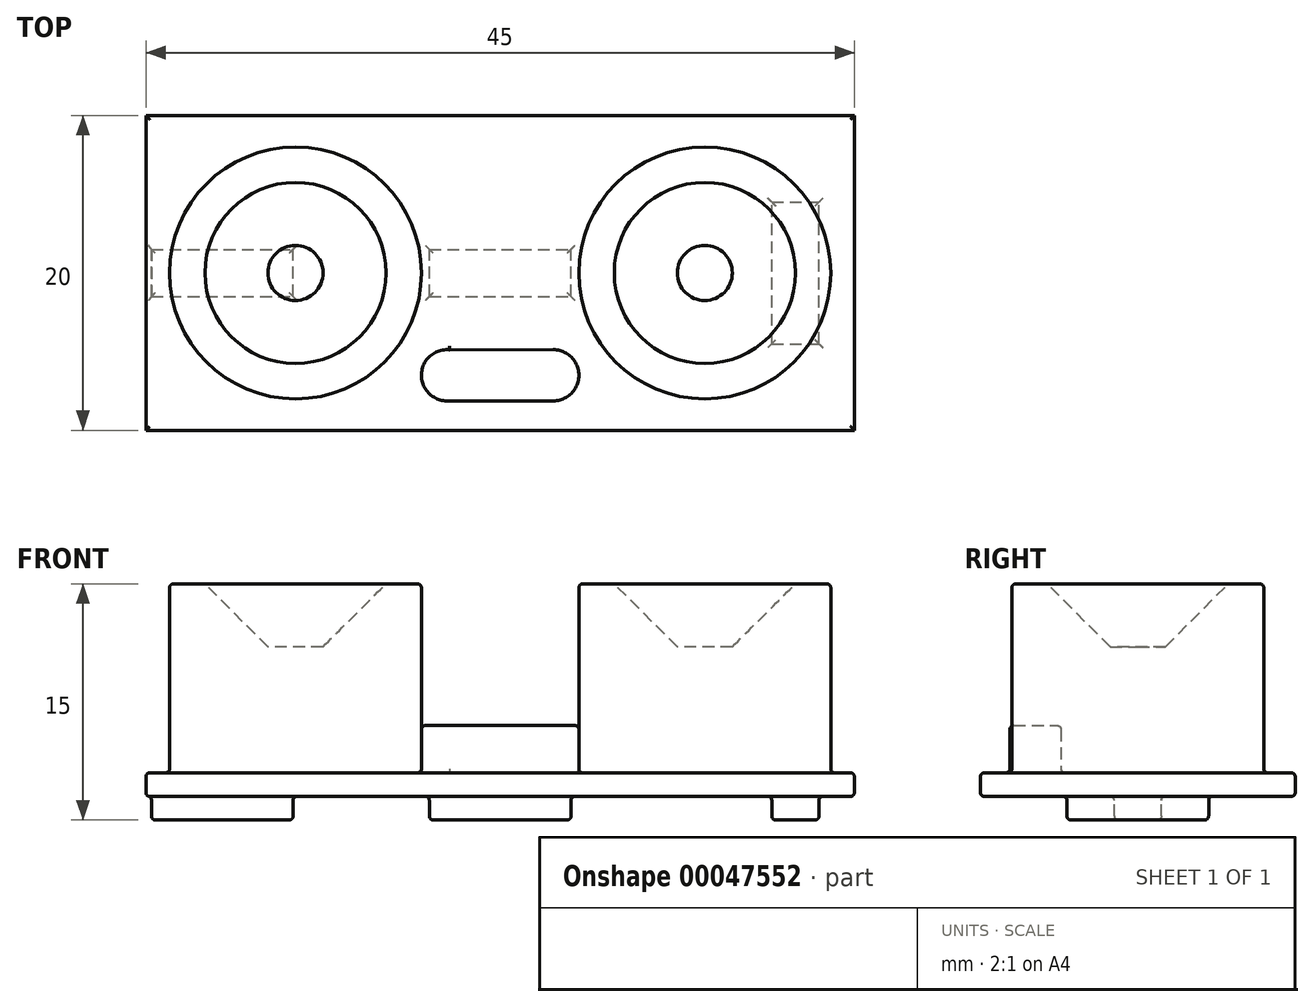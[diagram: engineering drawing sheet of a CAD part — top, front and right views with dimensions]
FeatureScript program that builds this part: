
annotation { "Feature Type Name" : "Feature", "Feature Type Description" : "" }
export const myFeature = defineFeature(function(context is Context, id is Id, definition is map)
    precondition{}
    {
        {
            var Q0;
            Q0=qCreatedBy(makeId("Top.planeOp"),FACE);
            var sketch = newSketch(context, id + "F0", { "sketchPlane" : qUnion([Q0])});
            skLineSegment(sketch, "E0.bottom", {"start": v(-22.5, 10) * mm, "end": v(22.5, 10) * mm});
            skLineSegment(sketch, "E0.top", {"start": v(-22.5, -10) * mm, "end": v(22.5, -10) * mm});
            skLineSegment(sketch, "E0.left", {"start": v(-22.5, 10) * mm, "end": v(-22.5, -10) * mm});
            skLineSegment(sketch, "E0.right", {"start": v(22.5, 10) * mm, "end": v(22.5, -10) * mm});
            skSolve(sketch);
        }
        {
            var Q0;
            Q0 = qSketchRegion(id + "F0", true);
            extrude(context, id + "F1", {"entities" : qUnion([Q0]), "depth" : 1.5 * mm});
        }
        {
            var Q0;
            Q0=makeQuery(id+"F1.opExtrude","CAP_FACE",FACE,{"disambiguationData":[OSD([sQuery(id+"F0.wireOp",EDGE,"E0.bottom"),sQuery(id+"F0.wireOp",EDGE,"E0.top"),sQuery(id+"F0.wireOp",EDGE,"E0.left"),sQuery(id+"F0.wireOp",EDGE,"E0.right")])],"isStart":false});
            var sketch = newSketch(context, id + "F2", { "sketchPlane" : qUnion([Q0])});
            skCircle(sketch, "E1", {"center": v(-13, 0) * mm, "radius": 8 * mm});
            skCircle(sketch, "E2", {"center": v(13, 0) * mm, "radius": 8 * mm});
            skSolve(sketch);
        }
        {
            var Q0;
            Q0 = qSketchRegion(id + "F2", true);
            extrude(context, id + "F3", {"entities" : qUnion([Q0]), "operationType" : NewBodyOperationType.ADD, "depth" : 12 * mm});
        }
        {
            var Q0;
            Q0=makeQuery(id+"F1.opExtrude","CAP_FACE",FACE,{"disambiguationData":[OSD([sQuery(id+"F0.wireOp",EDGE,"E0.bottom"),sQuery(id+"F0.wireOp",EDGE,"E0.top"),sQuery(id+"F0.wireOp",EDGE,"E0.left"),sQuery(id+"F0.wireOp",EDGE,"E0.right")])],"isStart":false});
            var sketch = newSketch(context, id + "F4", { "sketchPlane" : qUnion([Q0])});
            skArc(sketch, "E3", {"start": v(-3.22, -4.88) * mm, "mid": v(-5, -6.42) * mm, "end": v(-3.38, -8.12) * mm});
            skArc(sketch, "E4", {"start": v(3.38, -8.12) * mm, "mid": v(5, -6.5) * mm, "end": v(3.37, -4.88) * mm});
            skLineSegment(sketch, "E5", {"start": v(-3.54, -4.88) * mm, "end": v(3.38, -4.88) * mm});
            skLineSegment(sketch, "E6", {"start": v(-3.37, -8.12) * mm, "end": v(3.38, -8.12) * mm});
            skSolve(sketch);
        }
        {
            var Q0;
            Q0 = qSketchRegion(id + "F4", true);
            extrude(context, id + "F5", {"entities" : qUnion([Q0]), "operationType" : NewBodyOperationType.ADD, "depth" : 3 * mm});
        }
        {
            var Q0;
            Q0=makeQuery(id+"F3.opExtrude","CAP_FACE",FACE,{"disambiguationData":[OSD([sQuery(id+"F2.wireOp",EDGE,"E1")])],"isStart":false});
            var Q1;
            Q1=makeQuery(id+"F3.opExtrude","CAP_FACE",FACE,{"disambiguationData":[OSD([sQuery(id+"F2.wireOp",EDGE,"E2")])],"isStart":false});
            fillet(context, id + "F6", {"entities" : qUnion([Q0, Q1]), "radius" : .25 * mm, "tangentPropagation" : true, "allowEdgeOverflow" : false});
        }
        {
            var Q0;
            Q0=makeQuery(id+"F5.opExtrude","CAP_FACE",FACE,{"disambiguationData":[OSD([sQuery(id+"F4.wireOp",EDGE,"E3"),sQuery(id+"F4.wireOp",EDGE,"E4"),sQuery(id+"F4.wireOp",EDGE,"E5"),sQuery(id+"F4.wireOp",EDGE,"E6")])],"isStart":false});
            var Q1;
            Q1=makeQuery(id+"F5.opExtrude","SWEPT_FACE",FACE,{"disambiguationData":[OSD([sQuery(id+"F4.wireOp",EDGE,"E3")])]});
            var Q2;
            Q2=makeQuery(id+"F5.opExtrude","SWEPT_FACE",FACE,{"disambiguationData":[OSD([sQuery(id+"F4.wireOp",EDGE,"E6")])]});
            var Q3;
            Q3=makeQuery(id+"F5.opExtrude","SWEPT_FACE",FACE,{"disambiguationData":[OSD([sQuery(id+"F4.wireOp",EDGE,"E5")])]});
            var Q4;
            Q4=makeQuery(id+"F5.opExtrude","SWEPT_FACE",FACE,{"disambiguationData":[OSD([sQuery(id+"F4.wireOp",EDGE,"E4")])]});
            var Q5;
            Q5=makeQuery(id+"F3.opExtrude","SWEPT_FACE",FACE,{"disambiguationData":[OSD([sQuery(id+"F2.wireOp",EDGE,"E1")])]});
            var Q6;
            Q6=makeQuery(id+"F3.opExtrude","SWEPT_FACE",FACE,{"disambiguationData":[OSD([sQuery(id+"F2.wireOp",EDGE,"E2")])]});
            fillet(context, id + "F7", {"entities" : qUnion([Q0, Q1, Q2, Q3, Q4, Q5, Q6]), "radius" : .25 * mm, "tangentPropagation" : true, "allowEdgeOverflow" : false});
        }
        {
            var Q0;
            Q0=makeQuery(id+"F1.opExtrude","CAP_FACE",FACE,{"disambiguationData":[OSD([sQuery(id+"F0.wireOp",EDGE,"E0.bottom"),sQuery(id+"F0.wireOp",EDGE,"E0.top"),sQuery(id+"F0.wireOp",EDGE,"E0.left"),sQuery(id+"F0.wireOp",EDGE,"E0.right")])],"isStart":false});
            var Q1;
            Q1=makeQuery(id+"F1.opExtrude","CAP_FACE",FACE,{"disambiguationData":[OSD([sQuery(id+"F0.wireOp",EDGE,"E0.bottom"),sQuery(id+"F0.wireOp",EDGE,"E0.top"),sQuery(id+"F0.wireOp",EDGE,"E0.left"),sQuery(id+"F0.wireOp",EDGE,"E0.right")])],"isStart":true});
            fillet(context, id + "F8", {"entities" : qUnion([Q0, Q1]), "radius" : .25 * mm, "tangentPropagation" : true, "allowEdgeOverflow" : false});
        }
        {
            var Q0;
            Q0=makeQuery(id+"F1.opExtrude","CAP_FACE",FACE,{"disambiguationData":[OSD([sQuery(id+"F0.wireOp",EDGE,"E0.bottom"),sQuery(id+"F0.wireOp",EDGE,"E0.top"),sQuery(id+"F0.wireOp",EDGE,"E0.left"),sQuery(id+"F0.wireOp",EDGE,"E0.right")])],"isStart":true});
            var sketch = newSketch(context, id + "F9", { "sketchPlane" : qUnion([Q0])});
            skLineSegment(sketch, "E7.bottom", {"start": v(-4.5, 1.5) * mm, "end": v(4.5, 1.5) * mm});
            skLineSegment(sketch, "E7.top", {"start": v(-4.5, -1.5) * mm, "end": v(4.5, -1.5) * mm});
            skLineSegment(sketch, "E7.left", {"start": v(-4.5, 1.5) * mm, "end": v(-4.5, -1.5) * mm});
            skLineSegment(sketch, "E7.right", {"start": v(4.5, 1.5) * mm, "end": v(4.5, -1.5) * mm});
            skLineSegment(sketch, "E8.bottom", {"start": v(17.25, 4.5) * mm, "end": v(20.25, 4.5) * mm});
            skLineSegment(sketch, "E8.top", {"start": v(17.25, -4.5) * mm, "end": v(20.25, -4.5) * mm});
            skLineSegment(sketch, "E8.left", {"start": v(17.25, 4.5) * mm, "end": v(17.25, -4.5) * mm});
            skLineSegment(sketch, "E8.right", {"start": v(20.25, 4.5) * mm, "end": v(20.25, -4.5) * mm});
            skLineSegment(sketch, "E9.bottom", {"start": v(-22.15, 1.5) * mm, "end": v(-13.15, 1.5) * mm});
            skLineSegment(sketch, "E9.top", {"start": v(-22.15, -1.5) * mm, "end": v(-13.15, -1.5) * mm});
            skLineSegment(sketch, "E9.left", {"start": v(-22.15, 1.5) * mm, "end": v(-22.15, -1.5) * mm});
            skLineSegment(sketch, "E9.right", {"start": v(-13.15, 1.5) * mm, "end": v(-13.15, -1.5) * mm});
            skSolve(sketch);
        }
        {
            var Q0;
            Q0 = qSketchRegion(id + "F9", true);
            extrude(context, id + "F10", {"entities" : qUnion([Q0]), "operationType" : NewBodyOperationType.ADD, "depth" : 1.5 * mm});
        }
        {
            var Q0;
            Q0=makeQuery(id+"F1.opExtrude","CAP_FACE",FACE,{"disambiguationData":[OSD([sQuery(id+"F0.wireOp",EDGE,"E0.bottom"),sQuery(id+"F0.wireOp",EDGE,"E0.top"),sQuery(id+"F0.wireOp",EDGE,"E0.left"),sQuery(id+"F0.wireOp",EDGE,"E0.right")])],"isStart":true});
            var Q1;
            Q1=makeQuery(id+"F10.opExtrude","CAP_FACE",FACE,{"disambiguationData":[OSD([sQuery(id+"F9.wireOp",EDGE,"E9.bottom"),sQuery(id+"F9.wireOp",EDGE,"E9.top"),sQuery(id+"F9.wireOp",EDGE,"E9.left"),sQuery(id+"F9.wireOp",EDGE,"E9.right")])],"isStart":false});
            var Q2;
            Q2=makeQuery(id+"F10.opExtrude","CAP_FACE",FACE,{"disambiguationData":[OSD([sQuery(id+"F9.wireOp",EDGE,"E7.bottom"),sQuery(id+"F9.wireOp",EDGE,"E7.top"),sQuery(id+"F9.wireOp",EDGE,"E7.left"),sQuery(id+"F9.wireOp",EDGE,"E7.right")])],"isStart":false});
            var Q3;
            Q3=makeQuery(id+"F10.opExtrude","CAP_FACE",FACE,{"disambiguationData":[OSD([sQuery(id+"F9.wireOp",EDGE,"E8.bottom"),sQuery(id+"F9.wireOp",EDGE,"E8.top"),sQuery(id+"F9.wireOp",EDGE,"E8.left"),sQuery(id+"F9.wireOp",EDGE,"E8.right")])],"isStart":false});
            fillet(context, id + "F11", {"entities" : qUnion([Q0, Q1, Q2, Q3]), "radius" : .25 * mm, "tangentPropagation" : true, "allowEdgeOverflow" : false});
        }
        {
            var Q0;
            Q0=makeQuery(id+"F3.opExtrude","CAP_FACE",FACE,{"disambiguationData":[OSD([sQuery(id+"F2.wireOp",EDGE,"E1")])],"isStart":false});
            var sketch = newSketch(context, id + "F12", { "sketchPlane" : qUnion([Q0])});
            skCircle(sketch, "E10", {"center": v(-13, 0) * mm, "radius": 6.75 * mm});
            skSolve(sketch);
        }
        {
            var Q0;
            Q0 = qSketchRegion(id + "F12", true);
            extrude(context, id + "F13", {"entities" : qUnion([Q0]), "operationType" : NewBodyOperationType.REMOVE, "oppositeDirection" : true, "depth" : 4 * mm});
        }
        {
            var Q0;
            Q0=makeQuery(id+"F3.opExtrude","CAP_FACE",FACE,{"disambiguationData":[OSD([sQuery(id+"F2.wireOp",EDGE,"E2")])],"isStart":false});
            var sketch = newSketch(context, id + "F14", { "sketchPlane" : qUnion([Q0])});
            skCircle(sketch, "E11", {"center": v(13, 0) * mm, "radius": 6.75 * mm});
            skSolve(sketch);
        }
        {
            var Q0;
            Q0=makeQuery(id+"F14.imprint","IMPRINT",FACE,{"disambiguationData":[TD([[makeQuery(id+"F14.imprint","IMPRINT",EDGE,{"derivedFrom":sQuery(id+"F14.wireOp",EDGE,"E11")}),1.0]])]});
            extrude(context, id + "F15", {"entities" : qUnion([Q0]), "operationType" : NewBodyOperationType.REMOVE, "oppositeDirection" : true, "depth" : 4 * mm});
        }
        {
            var Q0;
            Q0=makeQuery(id+"F13.boolean.opBoolean","COPY",FACE,{"derivedFrom":makeQuery(id+"F13.opExtrude","CAP_FACE",FACE,{"disambiguationData":[OSD([sQuery(id+"F12.wireOp",EDGE,"E10")])],"isStart":false})});
            var Q1;
            Q1=makeQuery(id+"F15.boolean.opBoolean","COPY",FACE,{"derivedFrom":makeQuery(id+"F15.opExtrude","CAP_FACE",FACE,{"disambiguationData":[OSD([sQuery(id+"F14.wireOp",EDGE,"E11")])],"isStart":false})});
            chamfer(context, id + "F16", {"entities" : qUnion([Q0, Q1]), "width" : 5 * mm, "tangentPropagation" : true});
        }
    });
